# Revit family: Hager-Univers-IP41-vide-Saillie-NoHosted-CH-fr
name_source: partatom
category: Electrical Equipment
units: mm (PartAtom-declared; Revit-internal decimal feet)

## family parameters
Always vertical = Yes
Cut with Voids When Loaded = No
Panel Configuration = Two Columns, Circuits Across
Part Type = Panelboard
Room Calculation Point = No
Round Connector Dimension = Use Diameter
Shared = No
Work Plane-Based = Yes

## types (3) — shared parameters
Default Elevation = 1219 mm
EF000003 - mode de pose = EV000384 - saillie
EF000007 - couleur = EV000202 - blanc
EF000116 - numéro RAL = 9010
EF000118 - avec cadre/support de montage = No
EF000218 - profondeur d'encastrement = 84 mm  [stored 0.275591 ft]
EF000339 - type de capot = EV004216 - porte
EF001062 - finition CEM = No
EF001088 - possibilité de montage en saillie = No
EF001131 - profondeur intérieure = 84 mm  [stored 0.275591 ft]
EF001134 - rail DIN = No
EF001596 - matériau du boîtier/corps = EV000154 - autre
EF005474 - indice de protection (IP) = EV006416 - IP41
EF006244 - couvercle/porte transparent(e) = No
EF006306 - avec serrure = No
EF009212 - finition du couvercle = EV000116 - fermé
EF015776 - borne de mise à la terre = No
EF015777 - borne à conducteur neutre = No
EF015941 - porte pour transmission du signal = No
HG000002 - avec porte = Yes
HG000003 - Gamme = Univers
HG000005 - Epaisseur = 3 mm  [stored 0.00984252 ft]
HG000006 - Encastré = No
HG000009 - Porte à double battant = No
HG000010 - Portes asymétriques = No
HG000011 - Rangées du bas vides = No
HG000017 - Distance entre pôles = 18 mm  [stored 0.0590551 ft]
Manufacturer = Hager
Type Comments = Univers
zero-valued in all types: EF000266 - nombre de rangées, EF000332 - hauteur d'encastrement, EF002950 - largeur en nombre de modules, HG000001 - nombre de colonnes, HG000007 - Nombre de colonnes vides, HG000008 - Nombre de rangées vides

## per-type parameters (varying)
| type | EF000008 - largeur | EF000040 - hauteur | EF000049 - profondeur | EF000846 - largeur d'encastrement | EF004462 - type de fermeture | HG000004 - Référence fabricant | Model |
| Saillie IP41 L350 H350 P128 0 Modules - FB2008LN | 350 mm | 350 mm | 128 mm | 200 mm  [stored 0.656168 ft] | EV000154 - autre | FB2008LN | FB2008LN |
| Saillie IP41 L450 H450 P128 0 Modules - FB3008LN | 450 mm  [stored 1.47638 ft] | 450 mm  [stored 1.47638 ft] | 128 mm | 300 mm | EV000154 - autre | FB3008LN | FB3008LN |
| Saillie IP41 L540 H450 P148 0 Modules - FB3008SN | 540 mm  [stored 1.77165 ft] | 450 mm  [stored 1.47638 ft] | 148 mm  [stored 0.485564 ft] | 300 mm |  | FB3008SN | FB3008SN |

note: [stored X ft] marks values corroborated as IEEE doubles in the binary element streams (Revit-internal decimal feet)

## geometry (parser evidence)
native form markers: Sweep x13
no freeform markers — native parametric forms only
